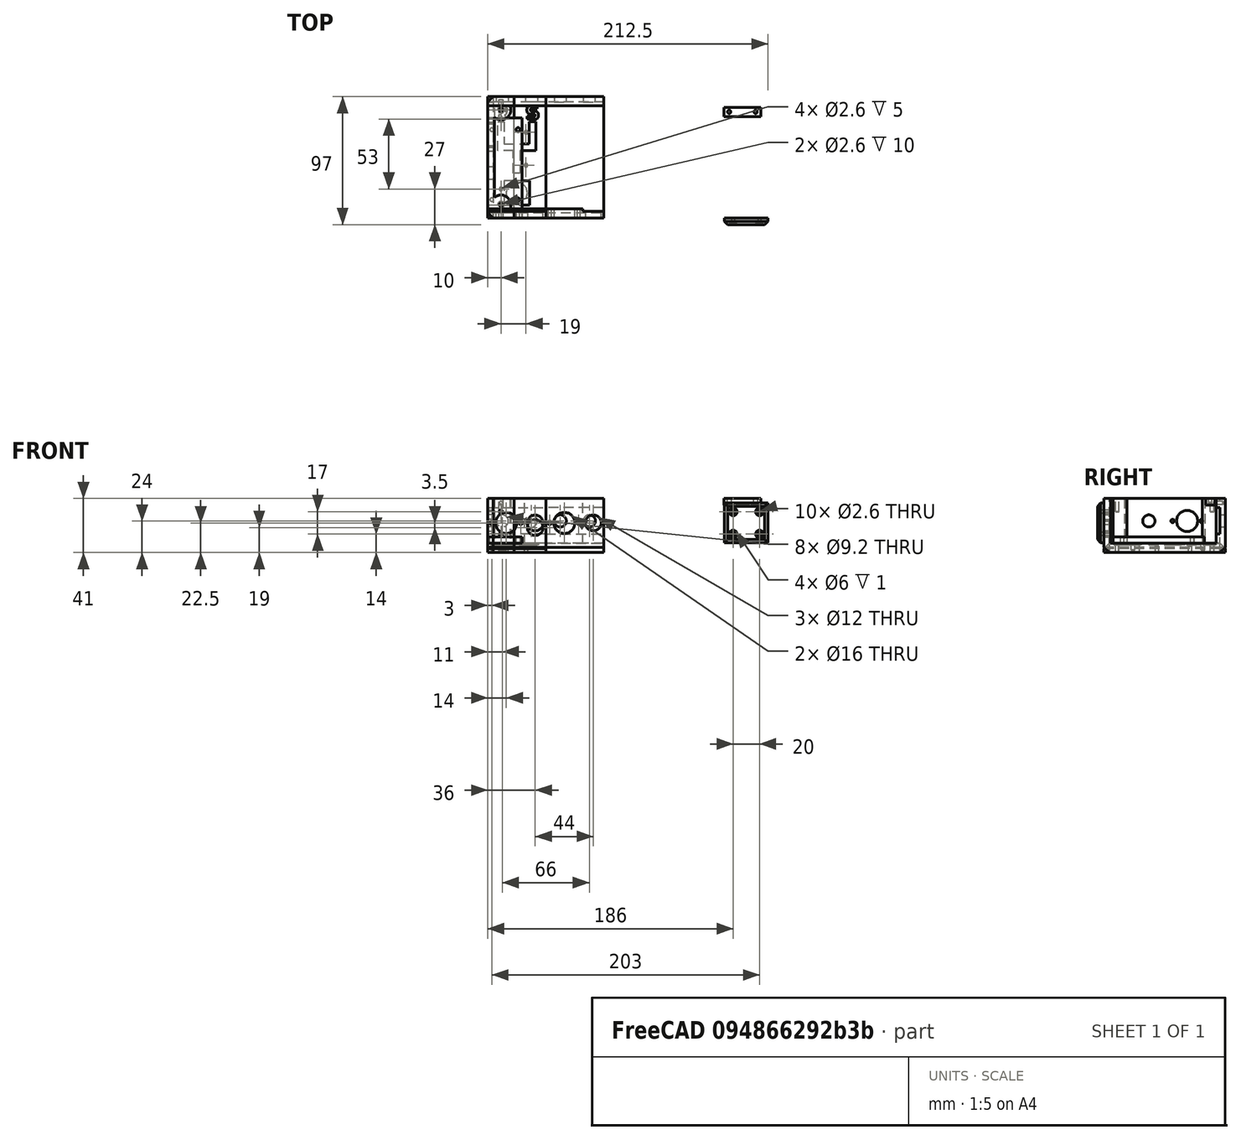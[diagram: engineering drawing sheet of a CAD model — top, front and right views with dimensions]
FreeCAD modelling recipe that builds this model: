
FCSTD DOCUMENT  (FreeCAD 1.0R39319 (Git))
Label: loop-switcher
License: All rights reserved
LicenseURL: https://en.wikipedia.org/wiki/All_rights_reserved
objects: App::Link×36, Sketcher::SketchObject×34, PartDesign::Pocket×26, PartDesign::Body×13, PartDesign::Pad×10, PartDesign::FeatureBase×6, PartDesign::Chamfer×5, Assembly::JointGroup×4, App::Part×4, Assembly::AssemblyObject×4, Assembly::AssemblyLink×4, Part::Part2DObjectPython×2, App::FeaturePython×1, Part::Mirroring×1
note: 219 computed .brp shape members not serialized (recipe doc carries the construction recipe); baked Part::Feature solids carry a one-line shape summary decoded from their .brp
EXTERNAL_REF file=perfboard-standoffs.FCStd obj=Assembly
EXTERNAL_REF file=perfboard-standoffs.FCStd obj=standoff
EXTERNAL_REF file=perfboard-standoffs.FCStd obj=standoff001
EXTERNAL_REF file=perfboard-standoffs.FCStd obj=standoff002
EXTERNAL_REF file=perfboard-standoffs.FCStd obj=standoff003

FEATURE [Sketcher::SketchObject] Sketch
  ArcFitTolerance = 1e-06
  AttachmentSupport = -> [XY_Plane]
  FullyConstrained = true
  MakeInternals = false
  MapMode = 5
  sketch-geometry (4):
    g0: LineSegment StartX=0 StartY=0 StartZ=0 EndX=44 EndY=0 EndZ=0
    g1: LineSegment StartX=44 StartY=0 StartZ=0 EndX=44 EndY=92 EndZ=0
    g2: LineSegment StartX=44 StartY=92 StartZ=0 EndX=0 EndY=92 EndZ=0
    g3: LineSegment StartX=0 StartY=92 StartZ=0 EndX=0 EndY=0 EndZ=0
  constraints (11):
    c: Coincident(g0,g1)
    c: Coincident(g1,g2)
    c: Coincident(g2,g3)
    c: Coincident(g3,g0)
    c: Horizontal(g0)
    c: Horizontal(g2)
    c: Vertical(g1)
    c: Vertical(g3)
    c: Distance(g1,g3) = 44
    c: Distance(g0,g2) = 92
    c: Coincident(g0,g-1)
FEATURE [PartDesign::Pad] Pad
  Direction = (0,0,1)
  Length = 7
  Length2 = 10
  Profile = -> Sketch
  ReferenceAxis = -> Sketch [N_Axis]
  Refine = true
  Suppressed = false
  Type = 0
FEATURE [Sketcher::SketchObject] Sketch001
  ArcFitTolerance = 1e-06
  AttachmentSupport = -> [Pad]
  ExternalGeometry = -> [Pad]
  FullyConstrained = true
  MakeInternals = false
  MapMode = 5
  Placement = pos=(0,0,7) rot=(0,0,1;0rad)
  sketch-geometry (8):
    g0: LineSegment StartX=0 StartY=92 StartZ=0 EndX=0 EndY=85 EndZ=0
    g1: LineSegment StartX=0 StartY=85 StartZ=0 EndX=44 EndY=85 EndZ=0
    g2: LineSegment StartX=44 StartY=85 StartZ=0 EndX=44 EndY=92 EndZ=0
    g3: LineSegment StartX=44 StartY=92 StartZ=0 EndX=0 EndY=92 EndZ=0
    g4: LineSegment StartX=0 StartY=0 StartZ=0 EndX=44 EndY=0 EndZ=0
    g5: LineSegment StartX=44 StartY=0 StartZ=0 EndX=44 EndY=7 EndZ=0
    g6: LineSegment StartX=44 StartY=7 StartZ=0 EndX=0 EndY=7 EndZ=0
    g7: LineSegment StartX=0 StartY=7 StartZ=0 EndX=0 EndY=0 EndZ=0
  constraints (22):
    c: Coincident(g0,g1)
    c: Coincident(g1,g2)
    c: Coincident(g2,g3)
    c: Coincident(g3,g0)
    c: Vertical(g0)
    c: Vertical(g2)
    c: Horizontal(g1)
    c: Horizontal(g3)
    c: Distance(g0,g2) = 44
    c: Distance(g1,g3) = 7
    c: Coincident(g0,g-3)
    c: Coincident(g4,g5)
    c: Coincident(g5,g6)
    c: Coincident(g6,g7)
    c: Coincident(g7,g4)
    c: Horizontal(g4)
    c: Horizontal(g6)
    c: Vertical(g5)
    c: Vertical(g7)
    c: Distance(g5,g7) = 44
    c: Distance(g4,g6) = 7
    c: Coincident(g4,g-1)
FEATURE [PartDesign::Pad] Pad001
  BaseFeature = -> Pad
  Direction = (0,0,1)
  Length = 34
  Length2 = 10
  Profile = -> Sketch001
  ReferenceAxis = -> Sketch001 [N_Axis]
  Refine = true
  Suppressed = false
  Type = 0
FEATURE [Sketcher::SketchObject] Sketch002
  ArcFitTolerance = 1e-06
  AttachmentSupport = -> [Pad001]
  ExternalGeometry = -> [Pad001]
  FullyConstrained = true
  MakeInternals = false
  MapMode = 5
  Placement = pos=(0,92,0) rot=(0,0.707107,0.707107;3.14159rad)
  sketch-geometry (2):
    g0: Circle CenterX=-33 CenterY=24 CenterZ=0 NormalX=0 NormalY=0 NormalZ=1 AngleXU=0 Radius=4.6
    g1: Circle CenterX=-11 CenterY=24 CenterZ=0 NormalX=0 NormalY=0 NormalZ=1 AngleXU=0 Radius=4.6
  constraints (6):
    c: Diameter(g0) = 9.2
    c: Diameter(g1) = 9.2
    c: DistanceX(g-4,g0) = 11
    c: DistanceX(g1,g-3) = 11
    c: DistanceY(g0,g-4) = 17
    c: DistanceY(g1,g-3) = 17
FEATURE [PartDesign::Pocket] Pocket
  BaseFeature = -> Pad001
  Direction = (0,-1,2e-16)
  Length = 10
  Length2 = 5
  Profile = -> Sketch002
  ReferenceAxis = -> Sketch002 [N_Axis]
  Refine = true
  Suppressed = false
  Type = 0
FEATURE [Sketcher::SketchObject] Sketch003
  ArcFitTolerance = 1e-06
  AttachmentSupport = -> [Pocket]
  ExternalGeometry = -> [Pocket]
  FullyConstrained = true
  MakeInternals = false
  MapMode = 5
  Placement = pos=(0,85,0) rot=(1,0,0;1.5708rad)
  sketch-geometry (5):
    g0: LineSegment StartX=-1.7e-15 StartY=14 StartZ=0 EndX=44 EndY=14 EndZ=0
    g1: LineSegment StartX=44 StartY=14 StartZ=0 EndX=44 EndY=34 EndZ=0
    g2: LineSegment StartX=44 StartY=34 StartZ=0 EndX=0 EndY=34 EndZ=0
    g3: LineSegment StartX=-1.7e-15 StartY=34 StartZ=0 EndX=-1.7e-15 EndY=14 EndZ=0
    g4: GeomPoint [constr] X=22 Y=24 Z=0
  constraints (13):
    c: Coincident(g0,g1)
    c: Coincident(g1,g2)
    c: Coincident(g2,g3)
    c: Coincident(g3,g0)
    c: Horizontal(g0)
    c: Horizontal(g2)
    c: Vertical(g1)
    c: Vertical(g3)
    c: Symmetric(g2,g0,g4)
    c: Distance(g1,g3) = 44
    c: Distance(g0,g2) = 20
    c: DistanceX(g4,g-4) = 22
    c: DistanceY(g4,g-4) = 17
FEATURE [PartDesign::Pocket] Pocket001
  BaseFeature = -> Pocket
  Direction = (0,1,-2e-16)
  Length = 3
  Length2 = 5
  Profile = -> Sketch003
  ReferenceAxis = -> Sketch003 [N_Axis]
  Refine = true
  Suppressed = false
  Type = 0
FEATURE [PartDesign::Chamfer] Chamfer
  Angle = 45
  Base = -> Pocket001 [Edge1,Edge3]
  BaseFeature = -> Pocket001
  ChamferType = 0
  FlipDirection = false
  Refine = true
  Size = 4
  Size2 = 1
  SupportTransform = false
  Suppressed = false
  UseAllEdges = false
FEATURE [PartDesign::Body] Body  label="base-module"
  AllowCompound = false
  Group = -> [Sketch,Pad,Sketch001,Pad001,Sketch002,Pocket,Sketch003,Pocket001,Chamfer]
  Origin = -> Origin
  Tip = -> Chamfer
FEATURE [Sketcher::SketchObject] Sketch004
  ArcFitTolerance = 1e-06
  AttachmentSupport = -> [XY_Plane003]
  FullyConstrained = true
  MakeInternals = false
  MapMode = 5
  sketch-geometry (4):
    g0: LineSegment StartX=0 StartY=0 StartZ=0 EndX=44 EndY=0 EndZ=0
    g1: LineSegment StartX=44 StartY=0 StartZ=0 EndX=44 EndY=92 EndZ=0
    g2: LineSegment StartX=44 StartY=92 StartZ=0 EndX=0 EndY=92 EndZ=0
    g3: LineSegment StartX=0 StartY=92 StartZ=0 EndX=0 EndY=0 EndZ=0
  constraints (11):
    c: Coincident(g0,g1)
    c: Coincident(g1,g2)
    c: Coincident(g2,g3)
    c: Coincident(g3,g0)
    c: Horizontal(g0)
    c: Horizontal(g2)
    c: Vertical(g1)
    c: Vertical(g3)
    c: Distance(g1,g3) = 44
    c: Distance(g0,g2) = 92
    c: Coincident(g0,g-1)
FEATURE [PartDesign::Pad] Pad002
  Direction = (0,0,1)
  Length = 7
  Length2 = 10
  Profile = -> Sketch004
  ReferenceAxis = -> Sketch004 [N_Axis]
  Refine = true
  Suppressed = false
  Type = 0
FEATURE [PartDesign::Chamfer] Chamfer001
  Angle = 45
  Base = -> Pad002 [Edge4,Edge10]
  BaseFeature = -> Pad002
  ChamferType = 0
  FlipDirection = false
  Refine = true
  Size = 4
  Size2 = 1
  SupportTransform = false
  Suppressed = false
  UseAllEdges = false
FEATURE [Sketcher::SketchObject] Sketch005
  ArcFitTolerance = 1e-06
  AttachmentOffset = pos=(0,5,0) rot=(0,0,1;0rad)
  AttachmentSupport = -> [Chamfer001]
  ExternalGeometry = -> [Chamfer001]
  FullyConstrained = true
  MakeInternals = false
  MapMode = 5
  Placement = pos=(0,5,7) rot=(0,0,1;0rad)
  sketch-geometry (12):
    g0: LineSegment StartX=7.5 StartY=68 StartZ=0 EndX=12.5 EndY=68 EndZ=0
    g1: LineSegment StartX=12.5 StartY=68 StartZ=0 EndX=12.5 EndY=51.1 EndZ=0
    g2: LineSegment StartX=12.5 StartY=51.1 StartZ=0 EndX=31.5 EndY=51.1 EndZ=0
    g3: LineSegment StartX=31.5 StartY=51.1 StartZ=0 EndX=31.5 EndY=68 EndZ=0
    g4: LineSegment StartX=31.5 StartY=68 StartZ=0 EndX=36.5 EndY=68 EndZ=0
    g5: LineSegment StartX=36.5 StartY=68 StartZ=0 EndX=36.5 EndY=46.1 EndZ=0
    g6: LineSegment StartX=36.5 StartY=46.1 StartZ=0 EndX=24.5 EndY=46.1 EndZ=0
    g7: LineSegment StartX=24.5 StartY=46.1 StartZ=0 EndX=24.5 EndY=29 EndZ=0
    g8: LineSegment StartX=24.5 StartY=29 StartZ=0 EndX=19.5 EndY=29 EndZ=0
    g9: LineSegment StartX=19.5 StartY=29 StartZ=0 EndX=19.5 EndY=46.1 EndZ=0
    g10: LineSegment StartX=19.5 StartY=46.1 StartZ=0 EndX=7.5 EndY=46.1 EndZ=0
    g11: LineSegment StartX=7.5 StartY=46.1 StartZ=0 EndX=7.5 EndY=68 EndZ=0
  constraints (36):
    c: Coincident(g0,g1)
    c: Coincident(g1,g2)
    c: Coincident(g2,g3)
    c: Coincident(g3,g4)
    c: Horizontal(g4)
    c: Coincident(g4,g5)
    c: Coincident(g5,g6)
    c: Coincident(g6,g7)
    c: Vertical(g7)
    c: Coincident(g7,g8)
    c: Coincident(g8,g9)
    c: Coincident(g9,g10)
    c: Coincident(g10,g11)
    c: Coincident(g11,g0)
    c: DistanceX(g0,g0) = 5
    c: DistanceX(g3,g4) = 5
    c: DistanceY(g0,g0) = 0
    c: DistanceY(g3,g0) = 0
    c: DistanceX(g10,g0) = 0
    c: DistanceX(g5,g4) = 0
    c: DistanceX(g2,g3) = 0
    c: DistanceX(g1,g0) = 0
    c: DistanceY(g2,g1) = 0
    c: DistanceY(g9,g1) = 5
    c: DistanceY(g5,g10) = 0
    c: DistanceX(g8,g7) = 5
    c: DistanceY(g7,g8) = 0
    c: DistanceY(g5,g6) = 0
    c: DistanceX(g8,g9) = 0
    c: DistanceX(g4,g-4) = 7.5
    c: DistanceX(g-3,g0) = 7.5
    c: DistanceX(g-1,g8) = 19.5
    c: DistanceY(g0,g-3) = 15
    c: DistanceY(g-1,g8) = 29
    c: DistanceY(g1,g0) = 16.9
    c: DistanceY(g10,g1) = 5
FEATURE [PartDesign::Pocket] Pocket002
  BaseFeature = -> Chamfer001
  Direction = (0,0,-1)
  Length = 1
  Length2 = 5
  Profile = -> Sketch005
  ReferenceAxis = -> Sketch005 [N_Axis]
  Refine = true
  Suppressed = false
  Type = 0
FEATURE [Sketcher::SketchObject] Sketch006
  ArcFitTolerance = 1e-06
  AttachmentSupport = -> [Pocket002]
  ExternalGeometry = -> [Pocket002]
  FullyConstrained = true
  MakeInternals = false
  MapMode = 5
  Placement = pos=(0,0,7) rot=(0,0,1;0rad)
  sketch-geometry (1):
    g0: Circle CenterX=22 CenterY=19 CenterZ=0 NormalX=0 NormalY=0 NormalZ=1 AngleXU=0 Radius=8
  constraints (3):
    c: Diameter(g0) = 16
    c: DistanceX(g-1,g0) = 22
    c: DistanceY(g-4,g0) = 15
FEATURE [PartDesign::Pocket] Pocket003
  BaseFeature = -> Pocket002
  Direction = (0,0,-1)
  Length = 10
  Length2 = 5
  Profile = -> Sketch006
  ReferenceAxis = -> Sketch006 [N_Axis]
  Refine = true
  Suppressed = false
  Type = 0
FEATURE [Sketcher::SketchObject] Sketch007
  ArcFitTolerance = 1e-06
  AttachmentSupport = -> [Pocket003]
  ExternalGeometry = -> [Pocket003]
  FullyConstrained = true
  MakeInternals = false
  MapMode = 5
  Placement = pos=(0,0,7) rot=(0,0,1;0rad)
  sketch-geometry (5):
    g0: LineSegment StartX=12.25 StartY=9.75 StartZ=0 EndX=31.75 EndY=9.75 EndZ=0
    g1: LineSegment StartX=31.75 StartY=9.75 StartZ=0 EndX=31.75 EndY=28.25 EndZ=0
    g2: LineSegment StartX=31.75 StartY=28.25 StartZ=0 EndX=12.25 EndY=28.25 EndZ=0
    g3: LineSegment StartX=12.25 StartY=28.25 StartZ=0 EndX=12.25 EndY=9.75 EndZ=0
    g4: GeomPoint [constr] X=22 Y=19 Z=0
  constraints (13):
    c: Coincident(g0,g1)
    c: Coincident(g1,g2)
    c: Coincident(g2,g3)
    c: Coincident(g3,g0)
    c: Horizontal(g0)
    c: Horizontal(g2)
    c: Vertical(g1)
    c: Vertical(g3)
    c: Symmetric(g2,g0,g4)
    c: Distance(g1,g3) = 19.5
    c: Distance(g0,g2) = 18.5
    c: DistanceY(g-3,g4) = 15
    c: DistanceX(g4,g-3) = 22
FEATURE [PartDesign::Pocket] Pocket004
  BaseFeature = -> Pocket003
  Direction = (0,0,-1)
  Length = 1
  Length2 = 5
  Profile = -> Sketch007
  ReferenceAxis = -> Sketch007 [N_Axis]
  Refine = true
  Suppressed = false
  Type = 0
FEATURE [Part::Part2DObjectPython] ShapeString  # Draft 2D object (typed FeaturePython)
  FontFile = <path>
  Fuse = false
  Justification = 4
  JustificationReference = 0
  KeepLeftMargin = false
  MakeFace = true
  ObliqueAngle = 0
  Placement = pos=(34,80,7) rot=(0,0,1;0rad)
  ScaleToSize = true
  Size = 10
  String = S
  Tracking = 0
FEATURE [PartDesign::Pocket] Pocket005
  BaseFeature = -> Pocket004
  Direction = (0,0,-1)
  Length = 1
  Length2 = 5
  Profile = -> ShapeString
  ReferenceAxis = -> ShapeString [N_Axis]
  Refine = true
  Suppressed = false
  Type = 0
FEATURE [Part::Part2DObjectPython] ShapeString001  # Draft 2D object (typed FeaturePython)
  FontFile = <path>
  Fuse = false
  Justification = 4
  JustificationReference = 0
  KeepLeftMargin = false
  MakeFace = true
  ObliqueAngle = 0
  Placement = pos=(10,80,7) rot=(0,0,1;0rad)
  ScaleToSize = true
  Size = 10
  String = R
  Tracking = 0
FEATURE [PartDesign::Pocket] Pocket006
  BaseFeature = -> Pocket005
  Direction = (0,0,-1)
  Length = 1
  Length2 = 5
  Profile = -> ShapeString001
  ReferenceAxis = -> ShapeString001 [N_Axis]
  Refine = true
  Suppressed = false
  Type = 0
FEATURE [PartDesign::Body] Body001  label="lid-module"
  AllowCompound = false
  Group = -> [Sketch004,Pad002,Chamfer001,Sketch005,Pocket002,Sketch006,Pocket003,Sketch007,Pocket004,ShapeString,Pocket005,ShapeString001,Pocket006]
  Origin = -> Origin003
  Tip = -> Pocket006
FEATURE [Sketcher::SketchObject] Sketch008
  ArcFitTolerance = 1e-06
  AttachmentSupport = -> [XY_Plane006]
  FullyConstrained = true
  MakeInternals = false
  MapMode = 5
  sketch-geometry (4):
    g0: LineSegment StartX=0 StartY=0 StartZ=0 EndX=20 EndY=0 EndZ=0
    g1: LineSegment StartX=20 StartY=0 StartZ=0 EndX=20 EndY=92 EndZ=0
    g2: LineSegment StartX=20 StartY=92 StartZ=0 EndX=0 EndY=92 EndZ=0
    g3: LineSegment StartX=0 StartY=92 StartZ=0 EndX=0 EndY=0 EndZ=0
  constraints (11):
    c: Coincident(g0,g1)
    c: Coincident(g1,g2)
    c: Coincident(g2,g3)
    c: Coincident(g3,g0)
    c: Horizontal(g0)
    c: Horizontal(g2)
    c: Vertical(g1)
    c: Vertical(g3)
    c: Distance(g1,g3) = 20
    c: Distance(g0,g2) = 92
    c: Coincident(g0,g-1)
FEATURE [PartDesign::Pad] Pad003
  Direction = (0,0,1)
  Length = 7
  Length2 = 10
  Profile = -> Sketch008
  ReferenceAxis = -> Sketch008 [N_Axis]
  Refine = true
  Suppressed = false
  Type = 0
FEATURE [Sketcher::SketchObject] Sketch009
  ArcFitTolerance = 1e-06
  AttachmentSupport = -> [Pad003]
  ExternalGeometry = -> [Pad003]
  FullyConstrained = true
  MakeInternals = false
  MapMode = 5
  Placement = pos=(0,0,7) rot=(0,0,1;0rad)
  sketch-geometry (12):
    g0: LineSegment StartX=20 StartY=92 StartZ=0 EndX=0 EndY=92 EndZ=0
    g1: LineSegment StartX=0 StartY=92 StartZ=0 EndX=0 EndY=85 EndZ=0
    g2: LineSegment StartX=0 StartY=85 StartZ=0 EndX=20 EndY=85 EndZ=0
    g3: LineSegment StartX=20 StartY=85 StartZ=0 EndX=20 EndY=92 EndZ=0
    g4: LineSegment StartX=0 StartY=0 StartZ=0 EndX=20 EndY=0 EndZ=0
    g5: LineSegment StartX=20 StartY=0 StartZ=0 EndX=20 EndY=7 EndZ=0
    g6: LineSegment StartX=20 StartY=7 StartZ=0 EndX=0 EndY=7 EndZ=0
    g7: LineSegment StartX=0 StartY=7 StartZ=0 EndX=0 EndY=0 EndZ=0
    g8: LineSegment StartX=0 StartY=7 StartZ=0 EndX=5 EndY=7 EndZ=0
    g9: LineSegment StartX=5 StartY=7 StartZ=0 EndX=5 EndY=85 EndZ=0
    g10: LineSegment StartX=5 StartY=85 StartZ=0 EndX=0 EndY=85 EndZ=0
    g11: LineSegment StartX=0 StartY=85 StartZ=0 EndX=0 EndY=7 EndZ=0
  constraints (33):
    c: Coincident(g0,g1)
    c: Coincident(g1,g2)
    c: Coincident(g2,g3)
    c: Coincident(g3,g0)
    c: Horizontal(g0)
    c: Horizontal(g2)
    c: Vertical(g1)
    c: Vertical(g3)
    c: Distance(g0,g2) = 7
    c: Coincident(g0,g-4)
    c: PointOnObject(g1,g-2)
    c: Coincident(g4,g5)
    c: Coincident(g5,g6)
    c: Coincident(g6,g7)
    c: Coincident(g7,g4)
    c: Horizontal(g4)
    c: Horizontal(g6)
    c: Vertical(g5)
    c: Vertical(g7)
    c: Distance(g4,g6) = 7
    c: Coincident(g4,g-1)
    c: PointOnObject(g5,g-4)
    c: Coincident(g8,g9)
    c: Coincident(g9,g10)
    c: Coincident(g10,g11)
    c: Coincident(g11,g8)
    c: Horizontal(g8)
    c: Horizontal(g10)
    c: Vertical(g9)
    c: Vertical(g11)
    c: Distance(g9,g11) = 5
    c: Coincident(g8,g6)
    c: PointOnObject(g9,g2)
FEATURE [PartDesign::Pad] Pad004
  BaseFeature = -> Pad003
  Direction = (0,0,1)
  Length = 34
  Length2 = 10
  Profile = -> Sketch009
  ReferenceAxis = -> Sketch009 [N_Axis]
  Refine = true
  Suppressed = false
  Type = 0
FEATURE [Sketcher::SketchObject] Sketch010
  ArcFitTolerance = 1e-06
  AttachmentSupport = -> [Pad004]
  ExternalGeometry = -> [Pad004]
  FullyConstrained = true
  MakeInternals = false
  MapMode = 5
  Placement = pos=(0,0,7) rot=(0,0,1;0rad)
  sketch-geometry (2):
    g0: Circle CenterX=10 CenterY=82 CenterZ=0 NormalX=0 NormalY=0 NormalZ=1 AngleXU=0 Radius=7.5
    g1: Circle CenterX=10 CenterY=10 CenterZ=0 NormalX=0 NormalY=0 NormalZ=1 AngleXU=0 Radius=7.5
  constraints (6):
    c: Diameter(g0) = 15
    c: DistanceY(g0,g-3) = 10
    c: DistanceX(g-3,g0) = 10
    c: Diameter(g1) = 15
    c: DistanceY(g-1,g1) = 10
    c: DistanceX(g-1,g1) = 10
FEATURE [PartDesign::Pad] Pad005
  BaseFeature = -> Pad004
  Direction = (0,0,1)
  Length = 34
  Length2 = 10
  Profile = -> Sketch010
  ReferenceAxis = -> Sketch010 [N_Axis]
  Refine = true
  Suppressed = false
  Type = 0
FEATURE [Sketcher::SketchObject] Sketch011
  ArcFitTolerance = 1e-06
  AttachmentSupport = -> [Pad005]
  ExternalGeometry = -> [Pad005]
  FullyConstrained = true
  MakeInternals = false
  MapMode = 5
  Placement = pos=(0,0,41) rot=(0,0,1;0rad)
  sketch-geometry (2):
    g0: Circle CenterX=10 CenterY=82 CenterZ=0 NormalX=0 NormalY=0 NormalZ=1 AngleXU=0 Radius=1.3
    g1: Circle CenterX=10 CenterY=10 CenterZ=0 NormalX=0 NormalY=0 NormalZ=1 AngleXU=0 Radius=1.3
  constraints (6):
    c: Diameter(g0) = 2.6
    c: Diameter(g1) = 2.6
    c: DistanceY(g-1,g1) = 10
    c: DistanceX(g-1,g1) = 10
    c: DistanceY(g0,g-3) = 10
    c: DistanceX(g-3,g0) = 10
FEATURE [PartDesign::Pocket] Pocket007
  BaseFeature = -> Pad005
  Direction = (0,0,-1)
  Length = 10
  Length2 = 5
  Profile = -> Sketch011
  ReferenceAxis = -> Sketch011 [N_Axis]
  Refine = true
  Suppressed = false
  Type = 0
FEATURE [PartDesign::Chamfer] Chamfer002
  Angle = 45
  Base = -> Pocket007 [Edge1,Edge7,Edge4,Edge14,Edge3]
  BaseFeature = -> Pocket007
  ChamferType = 0
  FlipDirection = false
  Refine = true
  Size = 4
  Size2 = 1
  SupportTransform = false
  Suppressed = false
  UseAllEdges = false
FEATURE [PartDesign::FeatureBase] Clone
  BaseFeature = -> Body
  Suppressed = false
FEATURE [Sketcher::SketchObject] Sketch012
  ArcFitTolerance = 1e-06
  AttachmentSupport = -> [Clone]
  ExternalGeometry = -> [Clone]
  FullyConstrained = true
  MakeInternals = false
  MapMode = 5
  Placement = pos=(0,0,7) rot=(0,0,1;0rad)
  sketch-geometry (2):
    g0: Circle CenterX=34 CenterY=75 CenterZ=0 NormalX=0 NormalY=0 NormalZ=1 AngleXU=0 Radius=1.3
    g1: Circle CenterX=34 CenterY=22 CenterZ=0 NormalX=0 NormalY=0 NormalZ=1 AngleXU=0 Radius=1.3
  constraints (6):
    c: Diameter(g0) = 2.6
    c: Diameter(g1) = 2.6
    c: DistanceY(g0,g-4) = 10
    c: DistanceX(g0,g-4) = 10
    c: DistanceY(g-3,g1) = 15
    c: DistanceX(g1,g-3) = 10
FEATURE [PartDesign::Pocket] Pocket008
  BaseFeature = -> Clone
  Direction = (0,0,-1)
  Length = 5
  Length2 = 5
  Profile = -> Sketch012
  ReferenceAxis = -> Sketch012 [N_Axis]
  Refine = true
  Suppressed = false
  Type = 0
FEATURE [Sketcher::SketchObject] Sketch013
  ArcFitTolerance = 1e-06
  AttachmentSupport = -> [Pocket008]
  ExternalGeometry = -> [Pocket008]
  FullyConstrained = true
  MakeInternals = false
  MapMode = 5
  Placement = pos=(0,0,0) rot=(1,0,0;1.5708rad)
  sketch-geometry (2):
    g0: Circle CenterX=34 CenterY=14 CenterZ=0 NormalX=0 NormalY=0 NormalZ=1 AngleXU=0 Radius=1.3
    g1: Circle CenterX=34 CenterY=31 CenterZ=0 NormalX=0 NormalY=0 NormalZ=1 AngleXU=0 Radius=1.3
  constraints (6):
    c: Diameter(g0) = 2.6
    c: Diameter(g1) = 2.6
    c: DistanceY(g1,g-5) = 10
    c: DistanceY(g-5,g0) = 10
    c: DistanceX(g0,g-5) = 10
    c: DistanceX(g1,g-5) = 10
FEATURE [PartDesign::Pocket] Pocket009
  BaseFeature = -> Pocket008
  Direction = (0,1,-2e-16)
  Length = 10
  Length2 = 5
  Profile = -> Sketch013
  ReferenceAxis = -> Sketch013 [N_Axis]
  Refine = true
  Suppressed = false
  Type = 0
FEATURE [App::Link] side  label="side001"
  LinkedObject = -> Body002
FEATURE [App::FeaturePython] GroundedJoint  # Assembly grounded joint (typed FeaturePython)
  ObjectToGround = -> side
FEATURE [Assembly::JointGroup] Joints
  Group = -> [GroundedJoint]
FEATURE [App::Link] base_module  label="base-module001"
  LinkPlacement = pos=(20,0,0) rot=(0,0,1;0rad)
  LinkedObject = -> Body
  Placement = pos=(20,0,0) rot=(0,0,1;0rad)
FEATURE [App::Link] base_module001  label="base-module002"
  LinkPlacement = pos=(64,0,0) rot=(0,0,1;0rad)
  LinkedObject = -> Body
  Placement = pos=(64,0,0) rot=(0,0,1;0rad)
FEATURE [App::Link] base_module002  label="base-module003"
  LinkPlacement = pos=(108,0,0) rot=(0,0,1;0rad)
  LinkedObject = -> Body
  Placement = pos=(108,0,0) rot=(0,0,1;0rad)
FEATURE [App::Link] split_module  label="split-module001"
  LinkPlacement = pos=(152,0,0) rot=(0,0,1;0rad)
  LinkedObject = -> Body003
  Placement = pos=(152,0,0) rot=(0,0,1;0rad)
FEATURE [Sketcher::SketchObject] Sketch014
  ArcFitTolerance = 1e-06
  AttachmentSupport = -> [Pocket009]
  ExternalGeometry = -> [Pocket009]
  FullyConstrained = true
  MakeInternals = false
  MapMode = 5
  Placement = pos=(0,85,0) rot=(1,0,0;1.5708rad)
  sketch-geometry (1):
    g0: Circle CenterX=34 CenterY=37.5 CenterZ=0 NormalX=0 NormalY=0 NormalZ=1 AngleXU=0 Radius=1.3
  constraints (3):
    c: Diameter(g0) = 2.6
    c: DistanceY(g0,g-3) = 3.5
    c: DistanceX(g0,g-3) = 10
FEATURE [PartDesign::Pocket] Pocket010
  BaseFeature = -> Pocket009
  Direction = (0,1,-2e-16)
  Length = 5
  Length2 = 5
  Profile = -> Sketch014
  ReferenceAxis = -> Sketch014 [N_Axis]
  Refine = true
  Suppressed = false
  Type = 0
FEATURE [PartDesign::Body] Body003  label="left-split"
  AllowCompound = false
  Group = -> [Clone,Sketch012,Pocket008,Sketch013,Pocket009,Sketch014,Pocket010]
  Origin = -> Origin007
  Tip = -> Pocket010
FEATURE [Assembly::JointGroup] Joints001
FEATURE [Sketcher::SketchObject] Sketch015
  ArcFitTolerance = 1e-06
  AttachmentSupport = -> [XY_Plane012]
  FullyConstrained = true
  MakeInternals = false
  MapMode = 5
  sketch-geometry (4):
    g0: LineSegment StartX=0 StartY=0 StartZ=0 EndX=20 EndY=0 EndZ=0
    g1: LineSegment StartX=20 StartY=0 StartZ=0 EndX=20 EndY=92 EndZ=0
    g2: LineSegment StartX=20 StartY=92 StartZ=0 EndX=0 EndY=92 EndZ=0
    g3: LineSegment StartX=0 StartY=92 StartZ=0 EndX=0 EndY=0 EndZ=0
  constraints (11):
    c: Coincident(g0,g1)
    c: Coincident(g1,g2)
    c: Coincident(g2,g3)
    c: Coincident(g3,g0)
    c: Horizontal(g0)
    c: Horizontal(g2)
    c: Vertical(g1)
    c: Vertical(g3)
    c: Distance(g1,g3) = 20
    c: Distance(g0,g2) = 92
    c: Coincident(g0,g-1)
FEATURE [PartDesign::Pad] Pad006
  Direction = (0,0,1)
  Length = 7
  Length2 = 10
  Profile = -> Sketch015
  ReferenceAxis = -> Sketch015 [N_Axis]
  Refine = true
  Suppressed = false
  Type = 0
FEATURE [PartDesign::Chamfer] Chamfer003
  Angle = 45
  Base = -> Pad006 [Edge10,Edge12,Edge4,Edge1,Edge8]
  BaseFeature = -> Pad006
  ChamferType = 0
  FlipDirection = false
  Refine = true
  Size = 4
  Size2 = 1
  SupportTransform = false
  Suppressed = false
  UseAllEdges = false
FEATURE [Sketcher::SketchObject] Sketch016
  ArcFitTolerance = 1e-06
  AttachmentSupport = -> [Chamfer003]
  ExternalGeometry = -> [Chamfer003]
  FullyConstrained = true
  MakeInternals = false
  MapMode = 5
  Placement = pos=(0,0,7) rot=(0,0,1;0rad)
  sketch-geometry (2):
    g0: Circle CenterX=10 CenterY=10 CenterZ=0 NormalX=0 NormalY=0 NormalZ=1 AngleXU=0 Radius=1.3
    g1: Circle CenterX=14 CenterY=82 CenterZ=0 NormalX=0 NormalY=0 NormalZ=1 AngleXU=0 Radius=1.3
  constraints (6):
    c: Diameter(g0) = 2.6
    c: Diameter(g1) = 2.6
    c: DistanceY(g1,g-3) = 10
    c: DistanceX(g-3,g1) = 10
    c: DistanceX(g-1,g0) = 10
    c: DistanceY(g-1,g0) = 10
FEATURE [PartDesign::Pocket] Pocket011
  BaseFeature = -> Chamfer003
  Direction = (0,0,-1)
  Length = 7
  Length2 = 5
  Profile = -> Sketch016
  ReferenceAxis = -> Sketch016 [N_Axis]
  Refine = true
  Suppressed = false
  Type = 0
FEATURE [Sketcher::SketchObject] Sketch017
  ArcFitTolerance = 1e-06
  AttachmentSupport = -> [Pocket011]
  FullyConstrained = true
  MakeInternals = false
  MapMode = 5
  Placement = pos=(0,0,7) rot=(0,0,1;0rad)
  sketch-geometry (2):
    g0: Circle CenterX=10 CenterY=10 CenterZ=0 NormalX=0 NormalY=0 NormalZ=1 AngleXU=0 Radius=2.5
    g1: Circle CenterX=10 CenterY=82 CenterZ=0 NormalX=0 NormalY=0 NormalZ=1 AngleXU=0 Radius=2.5
  constraints (6):
    c: Diameter(g0) = 5
    c: Diameter(g1) = 5
    c: DistanceY(g1,g-3) = 10
    c: DistanceY(g-1,g0) = 10
    c: DistanceX(g-1,g0) = 10
    c: DistanceX(g-3,g1) = 10
FEATURE [PartDesign::Pocket] Pocket012
  BaseFeature = -> Pocket011
  Direction = (0,0,-1)
  Length = 1
  Length2 = 5
  Profile = -> Sketch017
  ReferenceAxis = -> Sketch017 [N_Axis]
  Refine = true
  Suppressed = false
  Type = 0
FEATURE [PartDesign::Body] Body004  label="lid-side"
  AllowCompound = false
  Group = -> [Sketch015,Pad006,Chamfer003,Sketch016,Pocket011,Sketch017,Pocket012]
  Origin = -> Origin012
  Tip = -> Pocket012
FEATURE [PartDesign::FeatureBase] Clone001
  BaseFeature = -> Body001
  Suppressed = false
FEATURE [Sketcher::SketchObject] Sketch018
  ArcFitTolerance = 1e-06
  AttachmentSupport = -> [Clone001]
  ExternalGeometry = -> [Clone001]
  FullyConstrained = true
  MakeInternals = false
  MapMode = 5
  Placement = pos=(0,0,0) rot=(1,0,0;3.14159rad)
  sketch-geometry (2):
    g0: Circle CenterX=29 CenterY=-40 CenterZ=0 NormalX=0 NormalY=0 NormalZ=1 AngleXU=0 Radius=1.3
    g1: Circle CenterX=29 CenterY=-65 CenterZ=0 NormalX=0 NormalY=0 NormalZ=1 AngleXU=0 Radius=1.3
  constraints (6):
    c: Diameter(g0) = 2.6
    c: Diameter(g1) = 2.6
    c: DistanceX(g0,g1) = 0
    c: DistanceY(g1,g0) = 25
    c: DistanceY(g0,g-3) = 40
    c: DistanceX(g0,g-3) = 15
FEATURE [PartDesign::Pocket] Pocket013
  BaseFeature = -> Clone001
  Direction = (0,0,1)
  Length = 5
  Length2 = 5
  Profile = -> Sketch018
  ReferenceAxis = -> Sketch018 [N_Axis]
  Refine = true
  Suppressed = false
  Type = 0
FEATURE [PartDesign::Body] Body005  label="lid-split-left"
  AllowCompound = false
  Group = -> [Clone001,Sketch018,Pocket013]
  Origin = -> Origin013
  Tip = -> Pocket013
FEATURE [PartDesign::FeatureBase] Clone002
  BaseFeature = -> Body001
  Suppressed = false
FEATURE [Sketcher::SketchObject] Sketch019
  ArcFitTolerance = 1e-06
  AttachmentSupport = -> [Clone002]
  FullyConstrained = true
  MakeInternals = false
  MapMode = 5
  Placement = pos=(0,0,0) rot=(1,0,0;3.14159rad)
  sketch-geometry (2):
    g0: Circle CenterX=15 CenterY=-40 CenterZ=0 NormalX=0 NormalY=0 NormalZ=1 AngleXU=0 Radius=1.3
    g1: Circle CenterX=15 CenterY=-65 CenterZ=0 NormalX=0 NormalY=0 NormalZ=1 AngleXU=0 Radius=1.3
  constraints (6):
    c: Diameter(g0) = 2.6
    c: Diameter(g1) = 2.6
    c: DistanceX(g0,g1) = 0
    c: DistanceY(g1,g0) = 25
    c: DistanceX(g-1,g0) = 15
    c: DistanceY(g0,g-1) = 40
FEATURE [PartDesign::Pocket] Pocket014
  BaseFeature = -> Clone002
  Direction = (0,0,1)
  Length = 5
  Length2 = 5
  Profile = -> Sketch019
  ReferenceAxis = -> Sketch019 [N_Axis]
  Refine = true
  Suppressed = false
  Type = 0
FEATURE [PartDesign::Body] Body006  label="lid-split-right"
  AllowCompound = false
  Group = -> [Clone002,Sketch019,Pocket014]
  Origin = -> Origin014
  Tip = -> Pocket014
FEATURE [App::Part] Part001  label="lid-parts"
  Group = -> [Body001,Body004,Body005,Body006]
  Origin = -> Origin002
  Placement = pos=(0,100,0) rot=(0,0,1;0rad)
FEATURE [App::Link] lid_side  label="lid-side001"
  LinkedObject = -> Body004
FEATURE [App::Link] lid_module  label="lid-module001"
  LinkPlacement = pos=(20,0,0) rot=(0,0,1;0rad)
  LinkedObject = -> Body001
  Placement = pos=(20,0,0) rot=(0,0,1;0rad)
FEATURE [App::Link] lid_module001  label="lid-module002"
  LinkPlacement = pos=(64,0,0) rot=(0,0,1;0rad)
  LinkedObject = -> Body001
  Placement = pos=(64,0,0) rot=(0,0,1;0rad)
FEATURE [App::Link] lid_module002  label="lid-module003"
  LinkPlacement = pos=(108,0,0) rot=(0,0,1;0rad)
  LinkedObject = -> Body001
  Placement = pos=(108,0,0) rot=(0,0,1;0rad)
FEATURE [App::Link] lid_split_left  label="lid-split-left001"
  LinkPlacement = pos=(152,0,0) rot=(0,0,1;0rad)
  LinkedObject = -> Body005
  Placement = pos=(152,0,0) rot=(0,0,1;0rad)
FEATURE [Assembly::AssemblyObject] Assembly001  label="lid-left-half"
  Group = -> [Joints001,lid_side,lid_module,lid_module001,lid_module002,lid_split_left]
  Origin = -> Origin011
  Placement = pos=(0,120,0) rot=(0,0,1;0rad)
  Type = Assembly
FEATURE [Assembly::JointGroup] Joints002
FEATURE [App::Link] lid_side001  label="lid-side002"
  LinkPlacement = pos=(196,92,0) rot=(0,0,1;3.14159rad)
  LinkedObject = -> Body004
  Placement = pos=(196,92,0) rot=(0,0,1;3.14159rad)
FEATURE [App::Link] lid_module003  label="lid-module004"
  LinkPlacement = pos=(44,0,0) rot=(0,0,1;0rad)
  LinkedObject = -> Body001
  Placement = pos=(44,0,0) rot=(0,0,1;0rad)
FEATURE [App::Link] lid_module004  label="lid-module005"
  LinkPlacement = pos=(88,0,0) rot=(0,0,1;0rad)
  LinkedObject = -> Body001
  Placement = pos=(88,0,0) rot=(0,0,1;0rad)
FEATURE [App::Link] lid_module005  label="lid-module006"
  LinkPlacement = pos=(132,0,0) rot=(0,0,1;0rad)
  LinkedObject = -> Body001
  Placement = pos=(132,0,0) rot=(0,0,1;0rad)
FEATURE [App::Link] lid_split_right  label="lid-split-right001"
  LinkedObject = -> Body006
FEATURE [Assembly::AssemblyObject] Assembly002  label="lid-right-half"
  Group = -> [Joints002,lid_side001,lid_module003,lid_module004,lid_module005,lid_split_right]
  Origin = -> Origin015
  Placement = pos=(196,120,0) rot=(0,0,1;0rad)
  Type = Assembly
FEATURE [Sketcher::SketchObject] Sketch021
  ArcFitTolerance = 1e-06
  AttachmentSupport = -> [Chamfer002]
  ExternalGeometry = -> [Chamfer002]
  FullyConstrained = true
  MakeInternals = false
  MapMode = 5
  Placement = pos=(0,0,0) rot=(0.57735,-0.57735,-0.57735;2.0944rad)
  sketch-geometry (4):
    g0: Circle CenterX=-34 CenterY=24 CenterZ=0 NormalX=0 NormalY=0 NormalZ=1 AngleXU=0 Radius=4.6
    g1: Circle CenterX=-63 CenterY=24 CenterZ=0 NormalX=0 NormalY=0 NormalZ=1 AngleXU=0 Radius=8
    g2: Circle CenterX=-52 CenterY=24 CenterZ=0 NormalX=0 NormalY=0 NormalZ=1 AngleXU=0 Radius=1.3
    g3: Circle CenterX=-74 CenterY=24 CenterZ=0 NormalX=0 NormalY=0 NormalZ=1 AngleXU=0 Radius=1.3
  constraints (12):
    c: Diameter(g0) = 9.2
    c: DistanceY(g0,g-3) = 17
    c: Diameter(g1) = 16
    c: Diameter(g2) = 2.6
    c: Diameter(g3) = 2.6
    c: DistanceY(g2,g1) = 0
    c: DistanceY(g3,g1) = 0
    c: DistanceX(g1,g2) = 11
    c: DistanceX(g3,g1) = 11
    c: DistanceX(g0,g-3) = 30
    c: DistanceX(g-3,g1) = 25
    c: DistanceY(g3,g-3) = 17
FEATURE [PartDesign::Pocket] Pocket015
  BaseFeature = -> Chamfer002
  Direction = (1,0,0)
  Length = 7
  Length2 = 5
  Profile = -> Sketch021
  ReferenceAxis = -> Sketch021 [N_Axis]
  Refine = true
  Suppressed = false
  Type = 0
FEATURE [PartDesign::Body] Body002  label="side"
  AllowCompound = false
  Group = -> [Sketch008,Pad003,Sketch009,Pad004,Sketch010,Pad005,Sketch011,Pocket007,Chamfer002,Sketch021,Pocket015]
  Origin = -> Origin006
  Tip = -> Pocket015
FEATURE [Part::Mirroring] Part__Mirroring  label="right-split"
  Base = (0,0,0)
  Normal = (1,0,0)
  Placement = pos=(44,0,0) rot=(0,0,1;0rad)
  Source = -> Body003
FEATURE [Assembly::JointGroup] Joints003
FEATURE [App::Link] side001  label="side002"
  LinkPlacement = pos=(196,92,0) rot=(0,0,1;3.14159rad)
  LinkedObject = -> Body002
  Placement = pos=(196,92,0) rot=(0,0,1;3.14159rad)
FEATURE [App::Link] base_module003  label="base-module004"
  LinkPlacement = pos=(44,0,0) rot=(0,0,1;0rad)
  LinkedObject = -> Body
  Placement = pos=(44,0,0) rot=(0,0,1;0rad)
FEATURE [App::Link] base_module004  label="base-module005"
  LinkPlacement = pos=(88,0,0) rot=(0,0,1;0rad)
  LinkedObject = -> Body
  Placement = pos=(88,0,0) rot=(0,0,1;0rad)
FEATURE [App::Link] right_split  label="right-split001"
  LinkPlacement = pos=(44,0,0) rot=(0,0,1;0rad)
  LinkedObject = -> Part__Mirroring
  Placement = pos=(44,0,0) rot=(0,0,1;0rad)
FEATURE [PartDesign::FeatureBase] Clone003
  BaseFeature = -> Body
  Suppressed = false
FEATURE [Sketcher::SketchObject] Sketch023
  ArcFitTolerance = 1e-06
  AttachmentSupport = -> [Clone003]
  ExternalGeometry = -> [Clone003]
  FullyConstrained = true
  MakeInternals = false
  MapMode = 5
  Placement = pos=(0,0,0) rot=(1,0,0;1.5708rad)
  sketch-geometry (4):
    g0: Circle CenterX=14 CenterY=22.5 CenterZ=0 NormalX=0 NormalY=0 NormalZ=1 AngleXU=0 Radius=8
    g1: Circle CenterX=3 CenterY=22.5 CenterZ=0 NormalX=0 NormalY=0 NormalZ=1 AngleXU=0 Radius=1.3
    g2: Circle CenterX=25 CenterY=22.5 CenterZ=0 NormalX=0 NormalY=0 NormalZ=1 AngleXU=0 Radius=1.3
    g3: Circle CenterX=36 CenterY=22.5 CenterZ=0 NormalX=0 NormalY=0 NormalZ=1 AngleXU=0 Radius=6
  constraints (12):
    c: Diameter(g0) = 16
    c: DistanceY(g0,g-3) = 18.5
    c: Diameter(g1) = 2.6
    c: Diameter(g2) = 2.6
    c: DistanceY(g0,g1) = 0
    c: DistanceY(g0,g2) = 0
    c: DistanceX(g1,g0) = 11
    c: DistanceX(g0,g2) = 11
    c: DistanceX(g-3,g1) = 3
    c: Diameter(g3) = 12
    c: DistanceY(g3,g-3) = 18.5
    c: DistanceX(g3,g-3) = 8
FEATURE [PartDesign::Pocket] Pocket017
  BaseFeature = -> Clone003
  Direction = (0,1,-2e-16)
  Length = 8
  Length2 = 5
  Profile = -> Sketch023
  ReferenceAxis = -> Sketch023 [N_Axis]
  Refine = true
  Suppressed = false
  Type = 0
FEATURE [Sketcher::SketchObject] Sketch024
  ArcFitTolerance = 1e-06
  AttachmentSupport = -> [Pocket017]
  ExternalGeometry = -> [Pocket017]
  FullyConstrained = true
  MakeInternals = false
  MapMode = 5
  Placement = pos=(0,7,0) rot=(0,0.707107,0.707107;3.14159rad)
  sketch-geometry (4):
    g0: LineSegment StartX=-44 StartY=41 StartZ=0 EndX=-44 EndY=7 EndZ=0
    g1: LineSegment StartX=-44 StartY=7 StartZ=0 EndX=-28 EndY=7 EndZ=0
    g2: LineSegment StartX=-28 StartY=7 StartZ=0 EndX=-28 EndY=41 EndZ=0
    g3: LineSegment StartX=-28 StartY=41 StartZ=0 EndX=-44 EndY=41 EndZ=0
  constraints (11):
    c: Coincident(g0,g1)
    c: Coincident(g1,g2)
    c: Coincident(g2,g3)
    c: Coincident(g3,g0)
    c: Vertical(g0)
    c: Vertical(g2)
    c: Horizontal(g1)
    c: Horizontal(g3)
    c: Distance(g0,g2) = 16
    c: Coincident(g0,g-3)
    c: PointOnObject(g1,g-4)
FEATURE [PartDesign::Pocket] Pocket018
  BaseFeature = -> Pocket017
  Direction = (0,-1,2e-16)
  Length = 2
  Length2 = 5
  Profile = -> Sketch024
  ReferenceAxis = -> Sketch024 [N_Axis]
  Refine = true
  Suppressed = false
  Type = 0
FEATURE [PartDesign::Body] Body007  label="midi-in-and-power"
  AllowCompound = false
  Group = -> [Clone003,Sketch023,Pocket017,Sketch024,Pocket018]
  Origin = -> Origin020
  Tip = -> Pocket018
FEATURE [PartDesign::FeatureBase] Clone004
  Suppressed = false
FEATURE [Sketcher::SketchObject] Sketch029
  ArcFitTolerance = 1e-06
  AttachmentSupport = -> [Clone004]
  ExternalGeometry = -> [Clone004]
  FullyConstrained = true
  MakeInternals = false
  MapMode = 5
  Placement = pos=(0,0,0) rot=(1,0,0;1.5708rad)
  sketch-geometry (4):
    g0: Circle CenterX=14 CenterY=22.5 CenterZ=0 NormalX=0 NormalY=0 NormalZ=1 AngleXU=0 Radius=8
    g1: Circle CenterX=3 CenterY=22.5 CenterZ=0 NormalX=0 NormalY=0 NormalZ=1 AngleXU=0 Radius=1.3
    g2: Circle CenterX=25 CenterY=22.5 CenterZ=0 NormalX=0 NormalY=0 NormalZ=1 AngleXU=0 Radius=1.3
    g3: Circle CenterX=36 CenterY=22.5 CenterZ=0 NormalX=0 NormalY=0 NormalZ=1 AngleXU=0 Radius=6
  constraints (12):
    c: Diameter(g0) = 16
    c: DistanceY(g0,g-3) = 18.5
    c: Diameter(g1) = 2.6
    c: Diameter(g2) = 2.6
    c: DistanceY(g0,g1) = 0
    c: DistanceY(g0,g2) = 0
    c: DistanceX(g1,g0) = 11
    c: DistanceX(g0,g2) = 11
    c: DistanceX(g-3,g1) = 3
    c: Diameter(g3) = 12
    c: DistanceY(g3,g-3) = 18.5
    c: DistanceX(g3,g-3) = 8
FEATURE [PartDesign::Pocket] Pocket021
  BaseFeature = -> Clone004
  Direction = (0,1,-2e-16)
  Length = 8
  Length2 = 5
  Profile = -> Sketch029
  ReferenceAxis = -> Sketch029 [N_Axis]
  Refine = true
  Suppressed = false
  Type = 0
FEATURE [Sketcher::SketchObject] Sketch030
  ArcFitTolerance = 1e-06
  AttachmentSupport = -> [Pocket021]
  ExternalGeometry = -> [Pocket021]
  FullyConstrained = true
  MakeInternals = false
  MapMode = 5
  Placement = pos=(0,7,0) rot=(0,0.707107,0.707107;3.14159rad)
  sketch-geometry (4):
    g0: LineSegment StartX=-44 StartY=41 StartZ=0 EndX=-44 EndY=7 EndZ=0
    g1: LineSegment StartX=-44 StartY=7 StartZ=0 EndX=-28 EndY=7 EndZ=0
    g2: LineSegment StartX=-28 StartY=7 StartZ=0 EndX=-28 EndY=41 EndZ=0
    g3: LineSegment StartX=-28 StartY=41 StartZ=0 EndX=-44 EndY=41 EndZ=0
  constraints (11):
    c: Coincident(g0,g1)
    c: Coincident(g1,g2)
    c: Coincident(g2,g3)
    c: Coincident(g3,g0)
    c: Vertical(g0)
    c: Vertical(g2)
    c: Horizontal(g1)
    c: Horizontal(g3)
    c: Distance(g0,g2) = 16
    c: Coincident(g0,g-3)
    c: PointOnObject(g1,g-4)
FEATURE [PartDesign::Pocket] Pocket022
  BaseFeature = -> Pocket021
  Direction = (0,-1,2e-16)
  Length = 2
  Length2 = 5
  Profile = -> Sketch030
  ReferenceAxis = -> Sketch030 [N_Axis]
  Refine = true
  Suppressed = false
  Type = 0
FEATURE [PartDesign::Body] Body009  label="midi-in-and-power001"
  AllowCompound = false
  Group = -> [Clone004,Sketch029,Pocket021,Sketch030,Pocket022]
  Origin = -> Origin023
  Placement = pos=(44,0,0) rot=(0,0,1;0rad)
  Tip = -> Pocket022
FEATURE [App::Part] Part002
  Group = -> [Body007,Body009]
  Origin = -> Origin021
FEATURE [PartDesign::FeatureBase] Clone005
  BaseFeature = -> Body
  Suppressed = false
FEATURE [Sketcher::SketchObject] Sketch031
  ArcFitTolerance = 1e-06
  AttachmentSupport = -> [Clone005]
  ExternalGeometry = -> [Clone005]
  FullyConstrained = true
  MakeInternals = false
  MapMode = 5
  Placement = pos=(0,0,0) rot=(1,0,0;1.5708rad)
  sketch-geometry (1):
    g0: Circle CenterX=36 CenterY=19 CenterZ=0 NormalX=0 NormalY=0 NormalZ=1 AngleXU=0 Radius=6
  constraints (3):
    c: Diameter(g0) = 12
    c: DistanceX(g0,g-3) = 8
    c: DistanceY(g-3,g0) = 15
FEATURE [PartDesign::Pocket] Pocket023
  BaseFeature = -> Clone005
  Direction = (0,1,-2e-16)
  Length = 7
  Length2 = 5
  Profile = -> Sketch031
  ReferenceAxis = -> Sketch031 [N_Axis]
  Refine = true
  Suppressed = false
  Type = 0
FEATURE [Sketcher::SketchObject] Sketch032
  ArcFitTolerance = 1e-06
  AttachmentSupport = -> [Pocket023]
  ExternalGeometry = -> [Pocket023]
  FullyConstrained = true
  MakeInternals = false
  MapMode = 5
  Placement = pos=(0,7,0) rot=(0,0.707107,0.707107;3.14159rad)
  sketch-geometry (4):
    g0: LineSegment StartX=-44 StartY=41 StartZ=0 EndX=-44 EndY=7 EndZ=0
    g1: LineSegment StartX=-44 StartY=7 StartZ=0 EndX=0 EndY=7 EndZ=0
    g2: LineSegment StartX=0 StartY=7 StartZ=0 EndX=0 EndY=41 EndZ=0
    g3: LineSegment StartX=0 StartY=41 StartZ=0 EndX=-44 EndY=41 EndZ=0
  constraints (10):
    c: Coincident(g0,g1)
    c: Coincident(g1,g2)
    c: Coincident(g2,g3)
    c: Coincident(g3,g0)
    c: Vertical(g0)
    c: Vertical(g2)
    c: Horizontal(g1)
    c: Horizontal(g3)
    c: Coincident(g0,g-3)
    c: Coincident(g1,g-4)
FEATURE [PartDesign::Pocket] Pocket024
  BaseFeature = -> Pocket023
  Direction = (0,-1,2e-16)
  Length = 2
  Length2 = 5
  Profile = -> Sketch032
  ReferenceAxis = -> Sketch032 [N_Axis]
  Refine = true
  Suppressed = false
  Type = 0
FEATURE [PartDesign::Body] Body010  label="power-input-base-module"
  AllowCompound = false
  Group = -> [Clone005,Sketch031,Pocket023,Sketch032,Pocket024]
  Origin = -> Origin024
  Tip = -> Pocket024
FEATURE [App::Part] Part  label="base-parts"
  Group = -> [Body,Body002,Body003,Part__Mirroring,Part002,Body010]
  Origin = -> Origin001
FEATURE [App::Link] power_input_base_module  label="power-input-base-module001"
  LinkPlacement = pos=(132,0,0) rot=(0,0,1;0rad)
  LinkedObject = -> Body010
  Placement = pos=(132,0,0) rot=(0,0,1;0rad)
FEATURE [Sketcher::SketchObject] Sketch033
  ArcFitTolerance = 1e-06
  AttachmentSupport = -> [XY_Plane026]
  FullyConstrained = true
  MakeInternals = false
  MapMode = 5
  sketch-geometry (4):
    g0: LineSegment StartX=0 StartY=0 StartZ=0 EndX=26 EndY=0 EndZ=0
    g1: LineSegment StartX=26 StartY=0 StartZ=0 EndX=26 EndY=76 EndZ=0
    g2: LineSegment StartX=26 StartY=76 StartZ=0 EndX=0 EndY=76 EndZ=0
    g3: LineSegment StartX=0 StartY=76 StartZ=0 EndX=0 EndY=0 EndZ=0
  constraints (11):
    c: Coincident(g0,g1)
    c: Coincident(g1,g2)
    c: Coincident(g2,g3)
    c: Coincident(g3,g0)
    c: Horizontal(g0)
    c: Horizontal(g2)
    c: Vertical(g1)
    c: Vertical(g3)
    c: Distance(g1,g3) = 26
    c: Distance(g0,g2) = 76
    c: Coincident(g0,g-1)
FEATURE [PartDesign::Pad] Pad009
  Direction = (0,0,1)
  Length = 5
  Length2 = 10
  Profile = -> Sketch033
  ReferenceAxis = -> Sketch033 [N_Axis]
  Refine = true
  Suppressed = false
  Type = 0
FEATURE [Sketcher::SketchObject] Sketch034
  ArcFitTolerance = 1e-06
  AttachmentSupport = -> [Pad009]
  ExternalGeometry = -> [Pad009]
  FullyConstrained = true
  MakeInternals = false
  MapMode = 5
  Placement = pos=(0,0,5) rot=(0,0,1;0rad)
  sketch-geometry (4):
    g0: Circle CenterX=3 CenterY=14 CenterZ=0 NormalX=0 NormalY=0 NormalZ=1 AngleXU=0 Radius=1.3
    g1: Circle CenterX=23 CenterY=14 CenterZ=0 NormalX=0 NormalY=0 NormalZ=1 AngleXU=0 Radius=1.3
    g2: Circle CenterX=3 CenterY=67 CenterZ=0 NormalX=0 NormalY=0 NormalZ=1 AngleXU=0 Radius=1.3
    g3: Circle CenterX=23 CenterY=67 CenterZ=0 NormalX=0 NormalY=0 NormalZ=1 AngleXU=0 Radius=1.5
  constraints (12):
    c: Diameter(g0) = 2.6
    c: Diameter(g1) = 2.6
    c: Diameter(g2) = 2.6
    c: Diameter(g3) = 3
    c: DistanceX(g-3,g2) = 3
    c: DistanceX(g3,g-4) = 3
    c: DistanceY(g3,g-4) = 9
    c: DistanceY(g2,g-3) = 9
    c: DistanceY(g-1,g0) = 14
    c: DistanceX(g-1,g0) = 3
    c: DistanceX(g1,g-4) = 3
    c: DistanceY(g-4,g1) = 14
FEATURE [PartDesign::Pocket] Pocket025
  BaseFeature = -> Pad009
  Direction = (0,0,-1)
  Length = 5
  Length2 = 5
  Profile = -> Sketch034
  ReferenceAxis = -> Sketch034 [N_Axis]
  Refine = true
  Suppressed = false
  Type = 0
FEATURE [PartDesign::Body] Body011  label="bottom-splint"
  AllowCompound = false
  Group = -> [Sketch033,Pad009,Sketch034,Pocket025]
  Origin = -> Origin026
  Placement = pos=(0,0,7) rot=(0,0,1;0rad)
  Tip = -> Pocket025
FEATURE [Sketcher::SketchObject] Sketch035
  ArcFitTolerance = 1e-06
  AttachmentSupport = -> [XY_Plane027]
  FullyConstrained = true
  MakeInternals = false
  MapMode = 5
  sketch-geometry (4):
    g0: LineSegment StartX=0 StartY=0 StartZ=0 EndX=33 EndY=0 EndZ=0
    g1: LineSegment StartX=33 StartY=0 StartZ=0 EndX=33 EndY=30 EndZ=0
    g2: LineSegment StartX=33 StartY=30 StartZ=0 EndX=0 EndY=30 EndZ=0
    g3: LineSegment StartX=0 StartY=30 StartZ=0 EndX=0 EndY=0 EndZ=0
  constraints (11):
    c: Coincident(g0,g1)
    c: Coincident(g1,g2)
    c: Coincident(g2,g3)
    c: Coincident(g3,g0)
    c: Horizontal(g0)
    c: Horizontal(g2)
    c: Vertical(g1)
    c: Vertical(g3)
    c: Distance(g1,g3) = 33
    c: Distance(g0,g2) = 30
    c: Coincident(g0,g-1)
FEATURE [PartDesign::Pad] Pad010
  Direction = (0,0,1)
  Length = 5
  Length2 = 10
  Profile = -> Sketch035
  ReferenceAxis = -> Sketch035 [N_Axis]
  Refine = true
  Suppressed = false
  Type = 0
FEATURE [Sketcher::SketchObject] Sketch036
  ArcFitTolerance = 1e-06
  AttachmentSupport = -> [Pad010]
  ExternalGeometry = -> [Pad010]
  FullyConstrained = true
  MakeInternals = false
  MapMode = 5
  Placement = pos=(0,0,5) rot=(0,0,1;0rad)
  sketch-geometry (4):
    g0: Circle CenterX=6.5 CenterY=23.5 CenterZ=0 NormalX=0 NormalY=0 NormalZ=1 AngleXU=0 Radius=1.3
    g1: Circle CenterX=26.5 CenterY=23.5 CenterZ=0 NormalX=0 NormalY=0 NormalZ=1 AngleXU=0 Radius=1.3
    g2: Circle CenterX=6.5 CenterY=6.5 CenterZ=0 NormalX=0 NormalY=0 NormalZ=1 AngleXU=0 Radius=1.3
    g3: Circle CenterX=26.5 CenterY=6.5 CenterZ=0 NormalX=0 NormalY=0 NormalZ=1 AngleXU=0 Radius=1.3
  constraints (12):
    c: Diameter(g0) = 2.6
    c: Diameter(g1) = 2.6
    c: Diameter(g2) = 2.6
    c: Diameter(g3) = 2.6
    c: DistanceY(g1,g-4) = 6.5
    c: DistanceY(g0,g-3) = 6.5
    c: DistanceY(g-1,g2) = 6.5
    c: DistanceY(g-4,g3) = 6.5
    c: DistanceX(g3,g-4) = 6.5
    c: DistanceX(g1,g-4) = 6.5
    c: DistanceX(g-3,g0) = 6.5
    c: DistanceX(g-1,g2) = 6.5
FEATURE [PartDesign::Pocket] Pocket026
  BaseFeature = -> Pad010
  Direction = (0,0,-1)
  Length = 5
  Length2 = 5
  Profile = -> Sketch036
  ReferenceAxis = -> Sketch036 [N_Axis]
  Refine = true
  Suppressed = false
  Type = 0
FEATURE [Sketcher::SketchObject] Sketch037
  ArcFitTolerance = 1e-06
  AttachmentSupport = -> [XY_Plane028]
  FullyConstrained = true
  MakeInternals = false
  MapMode = 5
  sketch-geometry (4):
    g0: LineSegment StartX=0 StartY=0 StartZ=0 EndX=28 EndY=0 EndZ=0
    g1: LineSegment StartX=28 StartY=0 StartZ=0 EndX=28 EndY=7 EndZ=0
    g2: LineSegment StartX=28 StartY=7 StartZ=0 EndX=0 EndY=7 EndZ=0
    g3: LineSegment StartX=0 StartY=7 StartZ=0 EndX=0 EndY=0 EndZ=0
  constraints (11):
    c: Coincident(g0,g1)
    c: Coincident(g1,g2)
    c: Coincident(g2,g3)
    c: Coincident(g3,g0)
    c: Horizontal(g0)
    c: Horizontal(g2)
    c: Vertical(g1)
    c: Vertical(g3)
    c: Distance(g1,g3) = 28
    c: Distance(g0,g2) = 7
    c: Coincident(g0,g-1)
FEATURE [PartDesign::Pad] Pad011
  Direction = (0,0,1)
  Length = 5
  Length2 = 10
  Profile = -> Sketch037
  ReferenceAxis = -> Sketch037 [N_Axis]
  Refine = true
  Suppressed = false
  Type = 0
FEATURE [Sketcher::SketchObject] Sketch038
  ArcFitTolerance = 1e-06
  AttachmentSupport = -> [Pad011]
  ExternalGeometry = -> [Pad011]
  FullyConstrained = true
  MakeInternals = false
  MapMode = 5
  Placement = pos=(0,0,5) rot=(0,0,1;0rad)
  sketch-geometry (2):
    g0: Circle CenterX=24 CenterY=3.5 CenterZ=0 NormalX=0 NormalY=0 NormalZ=1 AngleXU=0 Radius=1.3
    g1: Circle CenterX=4 CenterY=3.5 CenterZ=0 NormalX=0 NormalY=0 NormalZ=1 AngleXU=0 Radius=1.3
  constraints (6):
    c: Diameter(g0) = 2.6
    c: Diameter(g1) = 2.6
    c: DistanceY(g0,g-4) = 3.5
    c: DistanceY(g1,g-3) = 3.5
    c: DistanceX(g0,g-4) = 4
    c: DistanceX(g-3,g1) = 4
FEATURE [PartDesign::Pocket] Pocket027
  BaseFeature = -> Pad011
  Direction = (0,0,-1)
  Length = 5
  Length2 = 5
  Profile = -> Sketch038
  ReferenceAxis = -> Sketch038 [N_Axis]
  Refine = true
  Suppressed = false
  Type = 0
FEATURE [PartDesign::Body] Body013  label="Body"
  AllowCompound = false
  Group = -> [Sketch037,Pad011,Sketch038,Pocket027]
  Origin = -> Origin028
  Placement = pos=(179,77,36) rot=(0,0,1;0rad)
  Tip = -> Pocket027
FEATURE [PartDesign::Chamfer] Chamfer005
  Angle = 45
  Base = -> Pocket026 [Edge10,Edge16,Edge7,Edge4]
  BaseFeature = -> Pocket026
  ChamferType = 0
  FlipDirection = false
  Refine = true
  Size = 2.5
  Size2 = 1
  SupportTransform = false
  Suppressed = false
  UseAllEdges = false
FEATURE [Sketcher::SketchObject] Sketch039
  ArcFitTolerance = 1e-06
  AttachmentSupport = -> [Chamfer005]
  ExternalGeometry = -> [Chamfer005]
  FullyConstrained = true
  MakeInternals = false
  MapMode = 5
  Placement = pos=(0,0,5) rot=(0,0,1;0rad)
  sketch-geometry (4):
    g0: Circle CenterX=6.5 CenterY=6.5 CenterZ=0 NormalX=0 NormalY=0 NormalZ=1 AngleXU=0 Radius=3
    g1: Circle CenterX=26.5 CenterY=6.5 CenterZ=0 NormalX=0 NormalY=0 NormalZ=1 AngleXU=0 Radius=3
    g2: Circle CenterX=26.5 CenterY=23.5 CenterZ=0 NormalX=0 NormalY=0 NormalZ=1 AngleXU=0 Radius=3
    g3: Circle CenterX=6.5 CenterY=23.5 CenterZ=0 NormalX=0 NormalY=0 NormalZ=1 AngleXU=0 Radius=3
  constraints (12):
    c: Diameter(g0) = 6
    c: Diameter(g1) = 6
    c: Diameter(g2) = 6
    c: Diameter(g3) = 6
    c: DistanceY(g3,g-3) = 6.5
    c: DistanceX(g-3,g3) = 6.5
    c: DistanceX(g2,g-4) = 6.5
    c: DistanceY(g2,g-4) = 6.5
    c: DistanceX(g1,g-4) = 6.5
    c: DistanceY(g-4,g1) = 6.5
    c: DistanceX(g-1,g0) = 6.5
    c: DistanceY(g-1,g0) = 6.5
FEATURE [PartDesign::Pocket] Pocket028
  BaseFeature = -> Chamfer005
  Direction = (0,0,-1)
  Length = 1
  Length2 = 5
  Profile = -> Sketch039
  ReferenceAxis = -> Sketch039 [N_Axis]
  Refine = true
  Suppressed = false
  Type = 0
FEATURE [PartDesign::Body] Body012  label="side-back-splint"
  AllowCompound = false
  Group = -> [Sketch035,Pad010,Sketch036,Pocket026,Chamfer005,Sketch039,Pocket028]
  Origin = -> Origin027
  Placement = pos=(179.5,0,7.5) rot=(1,0,0;1.5708rad)
  Tip = -> Pocket028
FEATURE [App::Part] Part003  label="splints"
  Group = -> [Body012,Body011,Body013]
  Origin = -> Origin025
FEATURE [App::Link] standoff016  label="standoff017"
  LinkedObject = -> <external perfboard-standoffs.FCStd>#standoff
FEATURE [App::Link] standoff017  label="standoff018"
  LinkPlacement = pos=(64.8,0,0) rot=(0,0,1;0rad)
  LinkedObject = -> <external perfboard-standoffs.FCStd>#standoff001
  Placement = pos=(64.8,0,0) rot=(0,0,1;0rad)
FEATURE [App::Link] standoff018  label="standoff019"
  LinkPlacement = pos=(0,45,0) rot=(0,0,1;0rad)
  LinkedObject = -> <external perfboard-standoffs.FCStd>#standoff002
  Placement = pos=(0,45,0) rot=(0,0,1;0rad)
FEATURE [App::Link] standoff019  label="standoff020"
  LinkPlacement = pos=(64.8,45,0) rot=(0,0,1;0rad)
  LinkedObject = -> <external perfboard-standoffs.FCStd>#standoff003
  Placement = pos=(64.8,45,0) rot=(0,0,1;0rad)
FEATURE [Assembly::AssemblyLink] standoffs004  label="standoffs002"
  Group = -> [standoff016,standoff017,standoff018,standoff019]
  LinkedObject = -> <external perfboard-standoffs.FCStd>#Assembly
  Origin = -> Origin029
  Placement = pos=(26,11,7) rot=(0,0,1;0rad)
  Rigid = true
FEATURE [App::Link] standoff020  label="standoff021"
  LinkedObject = -> <external perfboard-standoffs.FCStd>#standoff
FEATURE [App::Link] standoff021  label="standoff022"
  LinkPlacement = pos=(64.8,0,0) rot=(0,0,1;0rad)
  LinkedObject = -> <external perfboard-standoffs.FCStd>#standoff001
  Placement = pos=(64.8,0,0) rot=(0,0,1;0rad)
FEATURE [App::Link] standoff022  label="standoff023"
  LinkPlacement = pos=(0,45,0) rot=(0,0,1;0rad)
  LinkedObject = -> <external perfboard-standoffs.FCStd>#standoff002
  Placement = pos=(0,45,0) rot=(0,0,1;0rad)
FEATURE [App::Link] standoff023  label="standoff024"
  LinkPlacement = pos=(64.8,45,0) rot=(0,0,1;0rad)
  LinkedObject = -> <external perfboard-standoffs.FCStd>#standoff003
  Placement = pos=(64.8,45,0) rot=(0,0,1;0rad)
FEATURE [Assembly::AssemblyLink] standoffs005  label="standoffs003"
  Group = -> [standoff020,standoff021,standoff022,standoff023]
  LinkedObject = -> <external perfboard-standoffs.FCStd>#Assembly
  Origin = -> Origin030
  Placement = pos=(106,11,7) rot=(0,0,1;0rad)
  Rigid = true
FEATURE [Assembly::AssemblyObject] Assembly003  label="base-right-half"
  Group = -> [Joints003,side001,base_module003,base_module004,right_split,power_input_base_module,standoffs004,standoffs005]
  Origin = -> Origin016
  Placement = pos=(196,0,0) rot=(0,0,1;0rad)
  Type = Assembly
FEATURE [App::Link] standoff024  label="standoff025"
  LinkedObject = -> <external perfboard-standoffs.FCStd>#standoff
FEATURE [App::Link] standoff025  label="standoff026"
  LinkPlacement = pos=(64.8,0,0) rot=(0,0,1;0rad)
  LinkedObject = -> <external perfboard-standoffs.FCStd>#standoff001
  Placement = pos=(64.8,0,0) rot=(0,0,1;0rad)
FEATURE [App::Link] standoff026  label="standoff027"
  LinkPlacement = pos=(0,45,0) rot=(0,0,1;0rad)
  LinkedObject = -> <external perfboard-standoffs.FCStd>#standoff002
  Placement = pos=(0,45,0) rot=(0,0,1;0rad)
FEATURE [App::Link] standoff027  label="standoff028"
  LinkPlacement = pos=(64.8,45,0) rot=(0,0,1;0rad)
  LinkedObject = -> <external perfboard-standoffs.FCStd>#standoff003
  Placement = pos=(64.8,45,0) rot=(0,0,1;0rad)
FEATURE [Assembly::AssemblyLink] standoffs006  label="standoffs"
  Group = -> [standoff024,standoff025,standoff026,standoff027]
  LinkedObject = -> <external perfboard-standoffs.FCStd>#Assembly
  Origin = -> Origin031
  Placement = pos=(23,11,7) rot=(0,0,1;0rad)
  Rigid = true
FEATURE [App::Link] standoff028  label="standoff029"
  LinkedObject = -> <external perfboard-standoffs.FCStd>#standoff
FEATURE [App::Link] standoff029  label="standoff030"
  LinkPlacement = pos=(64.8,0,0) rot=(0,0,1;0rad)
  LinkedObject = -> <external perfboard-standoffs.FCStd>#standoff001
  Placement = pos=(64.8,0,0) rot=(0,0,1;0rad)
FEATURE [App::Link] standoff030  label="standoff031"
  LinkPlacement = pos=(0,45,0) rot=(0,0,1;0rad)
  LinkedObject = -> <external perfboard-standoffs.FCStd>#standoff002
  Placement = pos=(0,45,0) rot=(0,0,1;0rad)
FEATURE [App::Link] standoff031  label="standoff032"
  LinkPlacement = pos=(64.8,45,0) rot=(0,0,1;0rad)
  LinkedObject = -> <external perfboard-standoffs.FCStd>#standoff003
  Placement = pos=(64.8,45,0) rot=(0,0,1;0rad)
FEATURE [Assembly::AssemblyLink] standoffs007  label="standoffs001"
  Group = -> [standoff028,standoff029,standoff030,standoff031]
  LinkedObject = -> <external perfboard-standoffs.FCStd>#Assembly
  Origin = -> Origin032
  Placement = pos=(105,11,7) rot=(0,0,1;0rad)
  Rigid = true
FEATURE [Assembly::AssemblyObject] Assembly  label="base-left-half"
  Group = -> [Joints,side,GroundedJoint,base_module,base_module001,base_module002,split_module,standoffs006,standoffs007]
  Origin = -> Origin008
  Type = Assembly
note: 2 file-system paths scrubbed to <path> (originals preserved in the JSON sidecar)

RESOLVED EXTERNAL PARTS (link-assembly join: the EXTERNAL_REF files above that resolve inside this repo's crawl, each included once):
---- part perfboard-standoffs.FCStd = doc fcstd_f0f91593497c ----
FCSTD DOCUMENT  (FreeCAD 1.0R39319 (Git))
Label: perfboard-standoffs
License: All rights reserved
LicenseURL: https://en.wikipedia.org/wiki/All_rights_reserved
objects: App::Link×8, Sketcher::SketchObject×4, PartDesign::Body×2, Assembly::JointGroup×2, Assembly::AssemblyObject×2, PartDesign::Plane×1, PartDesign::AdditiveLoft×1, PartDesign::Pocket×1, App::FeaturePython×1, Assembly::AssemblyLink×1, PartDesign::Pad×1
note: 20 computed .brp shape members not serialized (recipe doc carries the construction recipe); baked Part::Feature solids carry a one-line shape summary decoded from their .brp

FEATURE [Sketcher::SketchObject] Sketch
  ArcFitTolerance = 1e-06
  AttachmentSupport = -> [XY_Plane001]
  FullyConstrained = true
  MakeInternals = false
  MapMode = 5
  sketch-geometry (1):
    g0: Circle CenterX=0 CenterY=0 CenterZ=0 NormalX=0 NormalY=0 NormalZ=1 AngleXU=0 Radius=4
  constraints (2):
    c: Diameter(g0) = 8
    c: Coincident(g0,g-1)
FEATURE [PartDesign::Plane] DatumPlane
  AttachmentOffset = pos=(0,0,4) rot=(0,0,1;0rad)
  AttachmentSupport = -> [Sketch]
  Length = 60
  MapMode = 2
  Placement = pos=(0,0,4) rot=(0,0,1;0rad)
  ResizeMode = 0
  Width = 60
FEATURE [Sketcher::SketchObject] Sketch001
  ArcFitTolerance = 1e-06
  AttachmentSupport = -> [DatumPlane]
  FullyConstrained = true
  MakeInternals = false
  MapMode = 5
  Placement = pos=(0,0,4) rot=(0,0,1;0rad)
  sketch-geometry (1):
    g0: Circle CenterX=0 CenterY=0 CenterZ=0 NormalX=0 NormalY=0 NormalZ=1 AngleXU=0 Radius=1.25
  constraints (2):
    c: Diameter(g0) = 2.5
    c: Coincident(g0,g-1)
FEATURE [PartDesign::AdditiveLoft] AdditiveLoft
  Closed = false
  Placement = pos=(0,0,4) rot=(0,0,1;0rad)
  Profile = -> Sketch001
  Refine = true
  Ruled = false
  Sections = -> [Sketch]
  Suppressed = false
FEATURE [Sketcher::SketchObject] Sketch002
  ArcFitTolerance = 1e-06
  AttachmentSupport = -> [AdditiveLoft]
  FullyConstrained = true
  MakeInternals = false
  MapMode = 5
  Placement = pos=(0,0,4) rot=(0,0,1;0rad)
  sketch-geometry (1):
    g0: Circle CenterX=0 CenterY=0 CenterZ=0 NormalX=0 NormalY=0 NormalZ=1 AngleXU=0 Radius=0.85
  constraints (2):
    c: Diameter(g0) = 1.7
    c: Coincident(g0,g-1)
FEATURE [PartDesign::Pocket] Pocket
  BaseFeature = -> AdditiveLoft
  Direction = (0,0,-1)
  Length = 5
  Length2 = 5
  Placement = pos=(0,0,4) rot=(0,0,1;0rad)
  Profile = -> Sketch002
  ReferenceAxis = -> Sketch002 [N_Axis]
  Refine = true
  Suppressed = false
  Type = 0
FEATURE [PartDesign::Body] Body  label="standoff"
  AllowCompound = false
  Group = -> [Sketch,DatumPlane,Sketch001,AdditiveLoft,Sketch002,Pocket]
  Origin = -> Origin001
  Tip = -> Pocket
FEATURE [App::Link] standoff  label="standoff001"
  LinkedObject = -> Body
FEATURE [App::FeaturePython] GroundedJoint  # Assembly grounded joint (typed FeaturePython)
  ObjectToGround = -> standoff
FEATURE [Assembly::JointGroup] Joints
  Group = -> [GroundedJoint]
FEATURE [App::Link] standoff001  label="standoff002"
  LinkPlacement = pos=(64.8,0,0) rot=(0,0,1;0rad)
  LinkedObject = -> Body
  Placement = pos=(64.8,0,0) rot=(0,0,1;0rad)
FEATURE [App::Link] standoff002  label="standoff003"
  LinkPlacement = pos=(0,45,0) rot=(0,0,1;0rad)
  LinkedObject = -> Body
  Placement = pos=(0,45,0) rot=(0,0,1;0rad)
FEATURE [App::Link] standoff003  label="standoff004"
  LinkPlacement = pos=(64.8,45,0) rot=(0,0,1;0rad)
  LinkedObject = -> Body
  Placement = pos=(64.8,45,0) rot=(0,0,1;0rad)
FEATURE [Assembly::AssemblyObject] Assembly  label="standoffs"
  Group = -> [Joints,standoff,GroundedJoint,standoff001,standoff002,standoff003]
  Origin = -> Origin
  Type = Assembly
FEATURE [Assembly::JointGroup] Joints001
FEATURE [App::Link] standoff004  label="standoff005"
  LinkedObject = -> standoff
FEATURE [App::Link] standoff005  label="standoff006"
  LinkPlacement = pos=(64.8,0,0) rot=(0,0,1;0rad)
  LinkedObject = -> standoff001
  Placement = pos=(64.8,0,0) rot=(0,0,1;0rad)
FEATURE [App::Link] standoff006  label="standoff007"
  LinkPlacement = pos=(0,45,0) rot=(0,0,1;0rad)
  LinkedObject = -> standoff002
  Placement = pos=(0,45,0) rot=(0,0,1;0rad)
FEATURE [App::Link] standoff007  label="standoff008"
  LinkPlacement = pos=(64.8,45,0) rot=(0,0,1;0rad)
  LinkedObject = -> standoff003
  Placement = pos=(64.8,45,0) rot=(0,0,1;0rad)
FEATURE [Assembly::AssemblyLink] standoffs  label="standoffs001"
  Group = -> [standoff004,standoff005,standoff006,standoff007]
  LinkedObject = -> Assembly
  Origin = -> Origin003
  Placement = pos=(5,6,2) rot=(0,0,1;0rad)
  Rigid = true
FEATURE [Sketcher::SketchObject] Sketch003
  ArcFitTolerance = 1e-06
  AttachmentSupport = -> [XY_Plane005]
  FullyConstrained = true
  MakeInternals = false
  MapMode = 5
  sketch-geometry (4):
    g0: LineSegment StartX=0 StartY=0 StartZ=0 EndX=75 EndY=0 EndZ=0
    g1: LineSegment StartX=75 StartY=0 StartZ=0 EndX=75 EndY=55 EndZ=0
    g2: LineSegment StartX=75 StartY=55 StartZ=0 EndX=0 EndY=55 EndZ=0
    g3: LineSegment StartX=0 StartY=55 StartZ=0 EndX=0 EndY=0 EndZ=0
  constraints (11):
    c: Coincident(g0,g1)
    c: Coincident(g1,g2)
    c: Coincident(g2,g3)
    c: Coincident(g3,g0)
    c: Horizontal(g0)
    c: Horizontal(g2)
    c: Vertical(g1)
    c: Vertical(g3)
    c: Distance(g1,g3) = 75
    c: Distance(g0,g2) = 55
    c: Coincident(g0,g-1)
FEATURE [PartDesign::Pad] Pad
  Direction = (0,0,1)
  Length = 2
  Length2 = 10
  Profile = -> Sketch003
  ReferenceAxis = -> Sketch003 [N_Axis]
  Refine = true
  Suppressed = false
  Type = 0
FEATURE [PartDesign::Body] Body001  label="Body"
  AllowCompound = false
  Group = -> [Sketch003,Pad]
  Origin = -> Origin005
  Tip = -> Pad
FEATURE [Assembly::AssemblyObject] Assembly001  label="print-test"
  Group = -> [Joints001,standoffs,Body001]
  Origin = -> Origin002
  Type = Assembly
